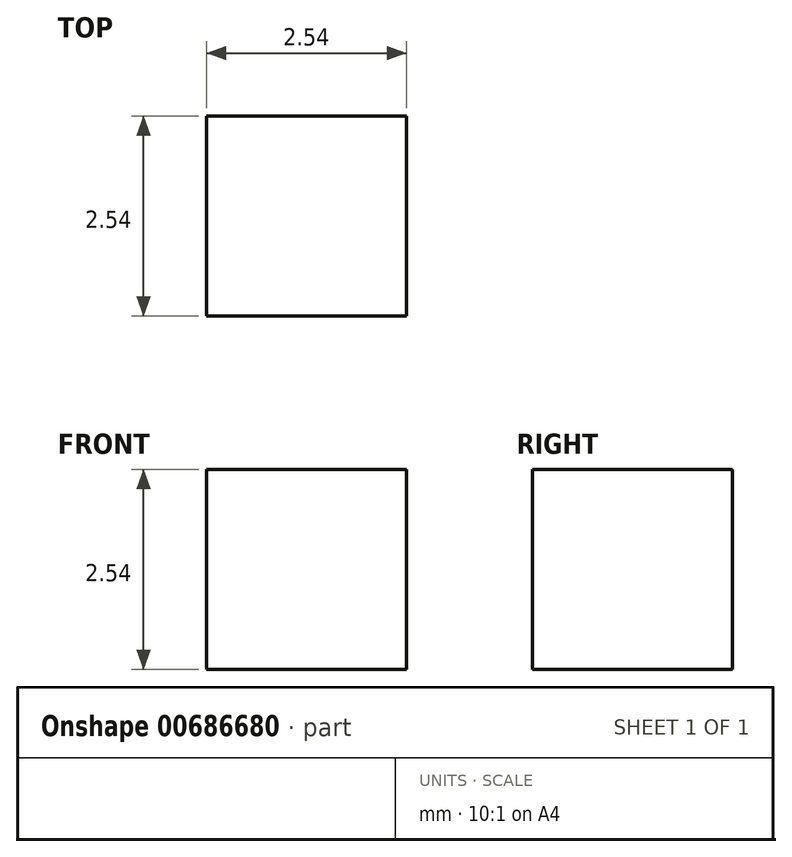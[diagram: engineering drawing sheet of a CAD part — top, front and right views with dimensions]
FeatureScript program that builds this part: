
annotation { "Feature Type Name" : "Feature", "Feature Type Description" : "" }
export const myFeature = defineFeature(function(context is Context, id is Id, definition is map)
    precondition{}
    {
        {
            var Q0;
            Q0=qCreatedBy(makeId("Top.planeOp"),FACE);
            var sketch = newSketch(context, id + "F0", { "sketchPlane" : qUnion([Q0])});
            skLineSegment(sketch, "E0.bottom", {"start": v(11.58, 26.76) * mm, "end": v(14.12, 26.76) * mm});
            skLineSegment(sketch, "E0.top", {"start": v(11.58, 24.22) * mm, "end": v(14.12, 24.22) * mm});
            skLineSegment(sketch, "E0.left", {"start": v(11.58, 26.76) * mm, "end": v(11.58, 24.22) * mm});
            skLineSegment(sketch, "E0.right", {"start": v(14.12, 26.76) * mm, "end": v(14.12, 24.22) * mm});
            skSolve(sketch);
        }
        {
            var Q0;
            Q0=makeQuery(id+"F0.imprint","IMPRINT",FACE,{"disambiguationData":[TD([[makeQuery(id+"F0.imprint","IMPRINT",EDGE,{"derivedFrom":sQuery(id+"F0.wireOp",EDGE,"E0.bottom")}),-1.0]])]});
            extrude(context, id + "F1", {"entities" : qUnion([Q0]), "depth" : 2.54 * mm, "offsetDistance" : 25.4 * mm});
        }
    });
